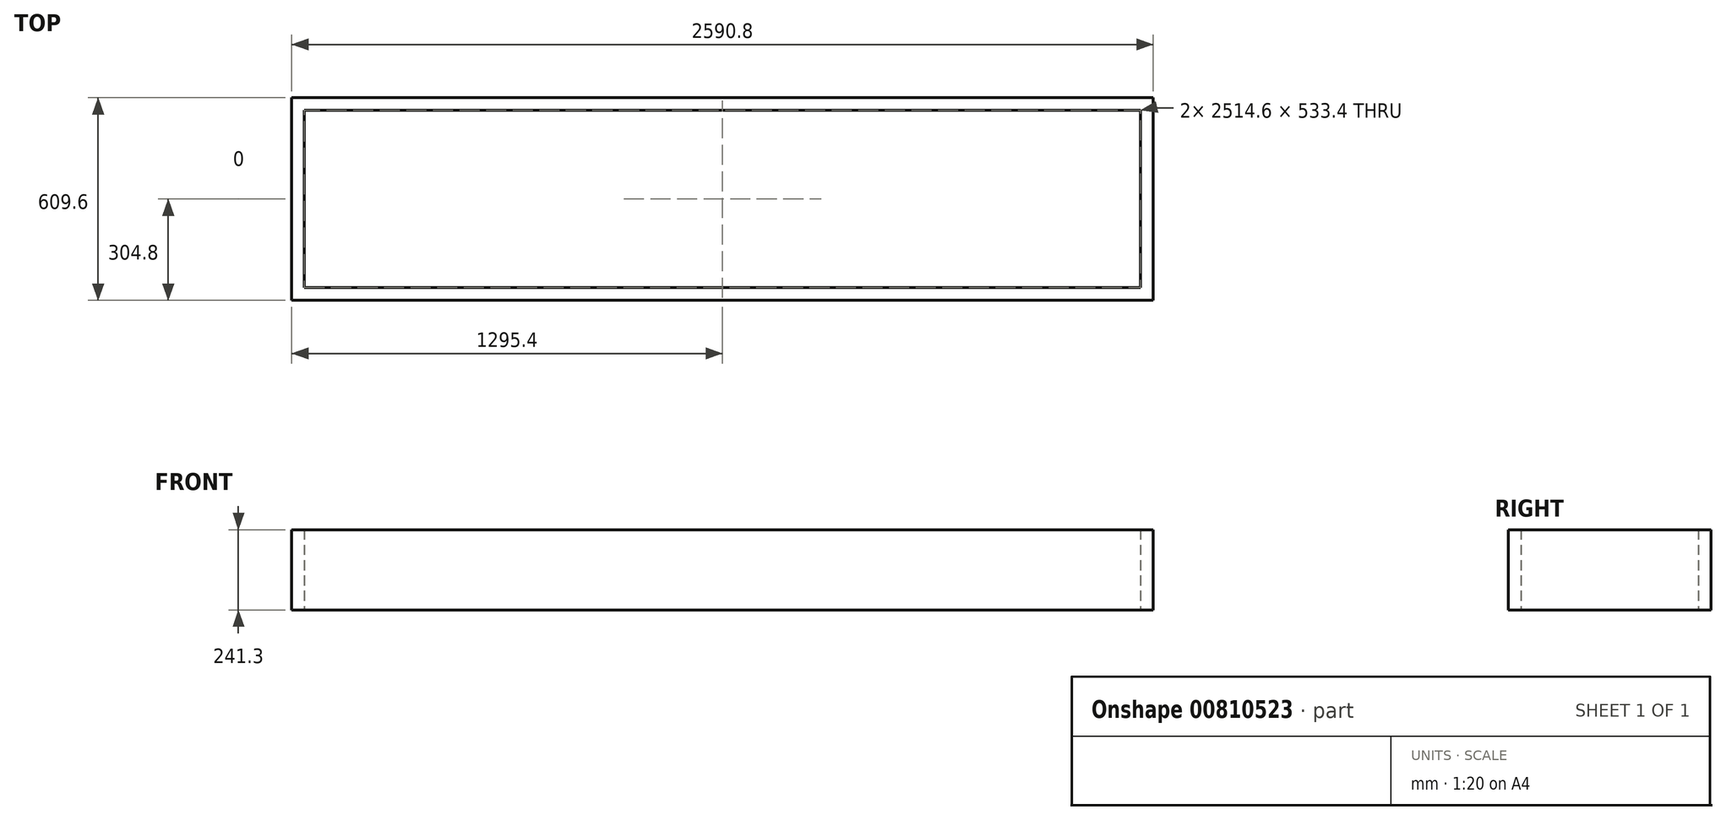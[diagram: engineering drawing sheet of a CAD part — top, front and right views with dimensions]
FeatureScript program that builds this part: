
annotation { "Feature Type Name" : "Feature", "Feature Type Description" : "" }
export const myFeature = defineFeature(function(context is Context, id is Id, definition is map)
    precondition{}
    {
        {
            var Q0;
            Q0=qCreatedBy(makeId("Top.planeOp"),FACE);
            var sketch = newSketch(context, id + "F0", { "sketchPlane" : qUnion([Q0])});
            skLineSegment(sketch, "E0.bottom", {"start": v(0, 0) * mm, "end": v(2590.8, 0) * mm, "construction": true});
            skLineSegment(sketch, "E0.top", {"start": v(0, -609.6) * mm, "end": v(2590.8, -609.6) * mm, "construction": true});
            skLineSegment(sketch, "E0.left", {"start": v(0, 0) * mm, "end": v(0, -609.6) * mm, "construction": true});
            skLineSegment(sketch, "E0.right", {"start": v(2590.8, 0) * mm, "end": v(2590.8, -609.6) * mm, "construction": true});
            skLineSegment(sketch, "E1.bottom", {"start": v(-75.31, -20.02) * mm, "end": v(-57.69, -20.02) * mm, "construction": true});
            skLineSegment(sketch, "E1.top", {"start": v(-75.31, -20.02) * mm, "end": v(-57.69, -20.02) * mm, "construction": true});
            skLineSegment(sketch, "E1.left", {"start": v(-75.31, -20.02) * mm, "end": v(-75.31, -20.02) * mm});
            skLineSegment(sketch, "E1.right", {"start": v(-57.69, -20.02) * mm, "end": v(-57.69, -20.02) * mm});
            skLineSegment(sketch, "E2.bottom", {"start": v(0, 0) * mm, "end": v(2590.8, 0) * mm});
            skLineSegment(sketch, "E2.top", {"start": v(0, -38.1) * mm, "end": v(2590.8, -38.1) * mm});
            skLineSegment(sketch, "E2.left", {"start": v(0, 0) * mm, "end": v(0, -38.1) * mm});
            skLineSegment(sketch, "E2.right", {"start": v(2590.8, 0) * mm, "end": v(2590.8, -38.1) * mm});
            skLineSegment(sketch, "E3.bottom", {"start": v(0, -609.6) * mm, "end": v(2590.8, -609.6) * mm});
            skLineSegment(sketch, "E3.top", {"start": v(0, -571.5) * mm, "end": v(2590.8, -571.5) * mm});
            skLineSegment(sketch, "E3.left", {"start": v(0, -609.6) * mm, "end": v(0, -571.5) * mm});
            skLineSegment(sketch, "E3.right", {"start": v(2590.8, -609.6) * mm, "end": v(2590.8, -571.5) * mm});
            skLineSegment(sketch, "E4.bottom", {"start": v(0, -38.1) * mm, "end": v(38.1, -38.1) * mm});
            skLineSegment(sketch, "E4.top", {"start": v(0, -571.5) * mm, "end": v(38.1, -571.5) * mm});
            skLineSegment(sketch, "E4.left", {"start": v(0, -38.1) * mm, "end": v(0, -571.5) * mm});
            skLineSegment(sketch, "E4.right", {"start": v(38.1, -38.1) * mm, "end": v(38.1, -571.5) * mm});
            skLineSegment(sketch, "E5.bottom", {"start": v(2590.8, -571.5) * mm, "end": v(2552.7, -571.5) * mm});
            skLineSegment(sketch, "E5.top", {"start": v(2590.8, -38.1) * mm, "end": v(2552.7, -38.1) * mm});
            skLineSegment(sketch, "E5.left", {"start": v(2590.8, -571.5) * mm, "end": v(2590.8, -38.1) * mm});
            skLineSegment(sketch, "E5.right", {"start": v(2552.7, -571.5) * mm, "end": v(2552.7, -38.1) * mm});
            skSolve(sketch);
        }
        {
            var Q0;
            Q0 = qSketchRegion(id + "F0", true);
            extrude(context, id + "F1", {"entities" : qUnion([Q0]), "depth" : 241.3 * mm, "offsetDistance" : 25.4 * mm});
        }
        {
            var Q0;
            Q0 = qSketchRegion(id + "F0", true);
            extrude(context, id + "F2", {"entities" : qUnion([Q0]), "depth" : 241.3 * mm, "offsetDistance" : 25.4 * mm});
        }
    });
